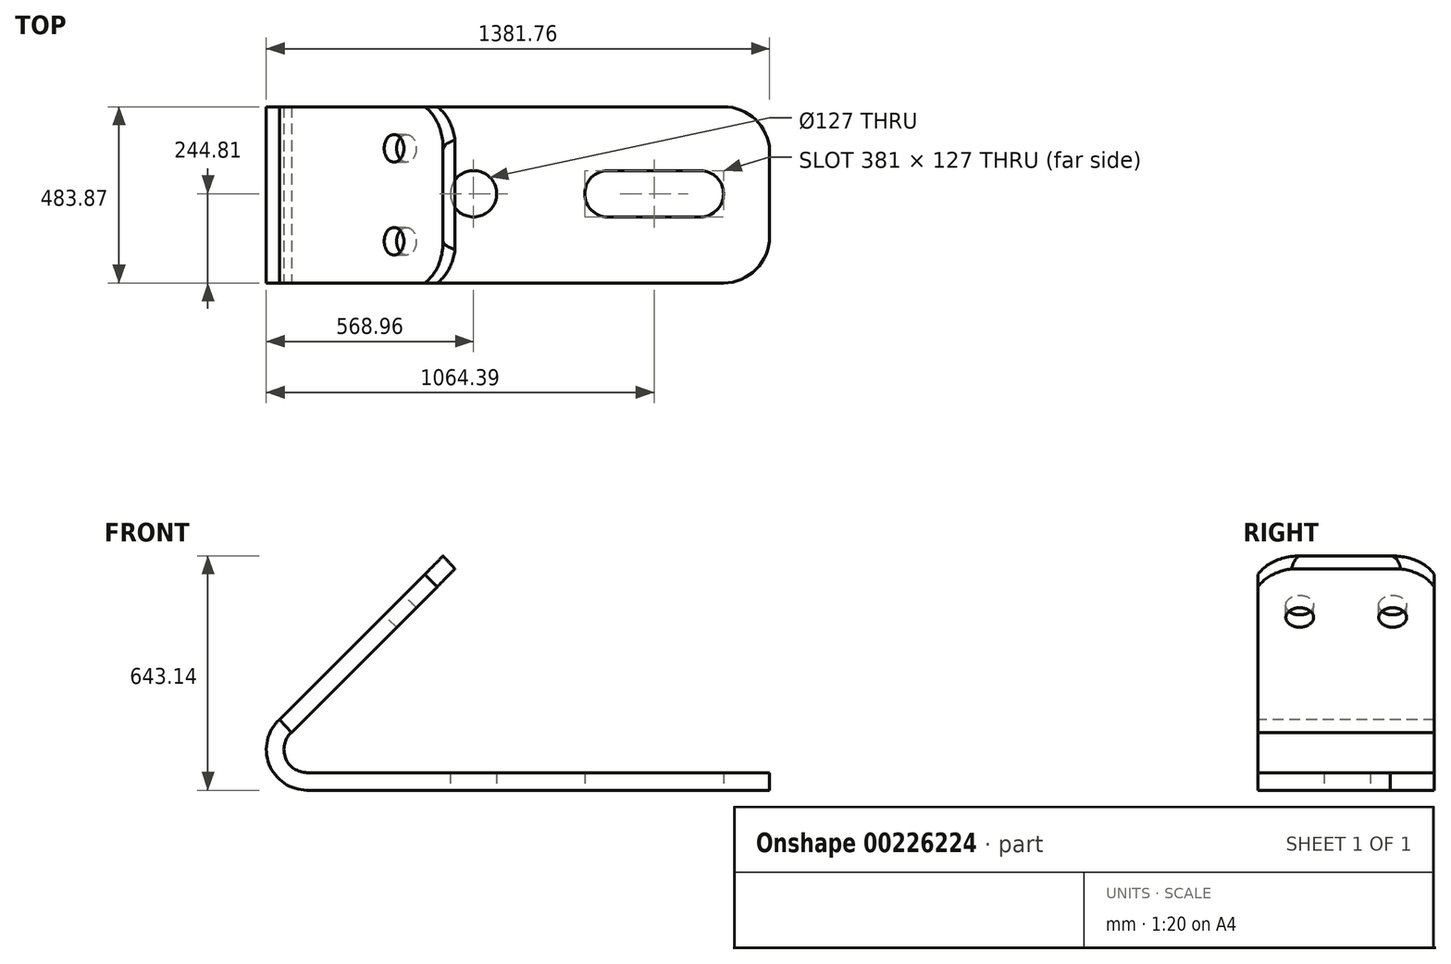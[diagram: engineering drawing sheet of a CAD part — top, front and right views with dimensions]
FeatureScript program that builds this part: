
annotation { "Feature Type Name" : "Feature", "Feature Type Description" : "" }
export const myFeature = defineFeature(function(context is Context, id is Id, definition is map)
    precondition{}
    {
        {
            var Q0;
            Q0=qCreatedBy(makeId("Top.planeOp"),FACE);
            var sketch = newSketch(context, id + "F0", { "sketchPlane" : qUnion([Q0])});
            skLineSegment(sketch, "E0", {"start": v(-457.2, 239.06) * mm, "end": v(-457.2, -244.8) * mm});
            skLineSegment(sketch, "E1", {"start": v(-457.2, -244.8) * mm, "end": v(685.93, -244.8) * mm});
            skLineSegment(sketch, "E2", {"start": v(-457.2, 239.06) * mm, "end": v(685.93, 239.06) * mm});
            skLineSegment(sketch, "E3", {"start": v(812.8, 117.8) * mm, "end": v(812.8, -117.8) * mm});
            skArc(sketch, "E4", {"start": v(812.8, 117.8) * mm, "mid": v(773.68, 203.87) * mm, "end": v(685.93, 239.06) * mm});
            skArc(sketch, "E5", {"start": v(685.93, -244.8) * mm, "mid": v(775.65, -207.56) * mm, "end": v(812.8, -117.8) * mm});
            skCircle(sketch, "E6", {"center": v(0, 0) * mm, "radius": 63.5 * mm});
            skLineSegment(sketch, "E7", {"start": v(0, 0) * mm, "end": v(908.2, 0) * mm, "construction": true});
            skLineSegment(sketch, "E8.bottom", {"start": v(368.43, 63.5) * mm, "end": v(622.43, 63.5) * mm});
            skLineSegment(sketch, "E8.top", {"start": v(368.43, -63.5) * mm, "end": v(622.43, -63.5) * mm});
            skPoint(sketch, "E8.middle", {"position": v(495.43, 0) * mm});
            skArc(sketch, "E9", {"start": v(368.43, 63.5) * mm, "mid": v(304.93, 0) * mm, "end": v(368.43, -63.5) * mm});
            skArc(sketch, "E10", {"start": v(622.43, -63.5) * mm, "mid": v(685.93, 0) * mm, "end": v(622.43, 63.5) * mm});
            skSolve(sketch);
        }
        {
            var Q0;
            Q0=makeQuery(id+"F0.imprint","IMPRINT",FACE,{"disambiguationData":[TD([[makeQuery(id+"F0.imprint","IMPRINT",EDGE,{"derivedFrom":sQuery(id+"F0.wireOp",EDGE,"E0")}),1.0]])]});
            extrude(context, id + "F1", {"entities" : qUnion([Q0]), "depth" : 48.26 * mm});
        }
        {
            var Q0;
            Q0=makeQuery(id+"F1.opExtrude","SWEPT_FACE",FACE,{"disambiguationData":[OSD([sQuery(id+"F0.wireOp",EDGE,"E1")])]});
            var sketch = newSketch(context, id + "F2", { "sketchPlane" : qUnion([Q0])});
            skArc(sketch, "E11", {"start": v(-532.74, 194.13) * mm, "mid": v(-561.35, 71.23) * mm, "end": v(-457.2, 0) * mm});
            skArc(sketch, "E12", {"start": v(-500.12, 158.56) * mm, "mid": v(-516.38, 88.73) * mm, "end": v(-457.2, 48.26) * mm});
            skLineSegment(sketch, "E13", {"start": v(-532.74, 194.13) * mm, "end": v(-500.12, 158.56) * mm});
            skSolve(sketch);
        }
        {
            var Q0;
            Q0 = qSketchRegion(id + "F2", true);
            var Q1;
            Q1=makeQuery(id+"F2.imprint","IMPRINT",FACE,{"disambiguationData":[TD([[makeQuery(id+"F2.imprint","IMPRINT",EDGE,{"derivedFrom":sQuery(id+"F2.wireOp",EDGE,"E11")}),1.0]])]});
            extrude(context, id + "F3", {"entities" : qUnion([Q0, Q1]), "oppositeDirection" : true, "depth" : 483.87 * mm});
        }
        {
            var Q0;
            Q0 = qSketchRegion(id + "F2", true);
            var Q1;
            Q1=makeQuery(id+"F3.opExtrude","CAP_FACE",FACE,{"disambiguationData":[OSD([sQuery(id+"F0.wireOp",EDGE,"E0"),sQuery(id+"F0.wireOp",EDGE,"E1"),sQuery(id+"F2.wireOp",EDGE,"E11"),sQuery(id+"F2.wireOp",EDGE,"E12"),sQuery(id+"F2.wireOp",EDGE,"E13")])],"isStart":true});
            extrude(context, id + "F4", {"entities" : qUnion([Q0, Q1]), "operationType" : NewBodyOperationType.ADD, "oppositeDirection" : true, "depth" : 483.87 * mm});
        }
        {
            var Q0;
            Q0=makeQuery(id+"F3.opExtrude","CAP_FACE",FACE,{"disambiguationData":[OSD([sQuery(id+"F0.wireOp",EDGE,"E0"),sQuery(id+"F0.wireOp",EDGE,"E1"),sQuery(id+"F2.wireOp",EDGE,"E11"),sQuery(id+"F2.wireOp",EDGE,"E12"),sQuery(id+"F2.wireOp",EDGE,"E13")])],"isStart":true});
            var sketch = newSketch(context, id + "F5", { "sketchPlane" : qUnion([Q0])});
            skLineSegment(sketch, "E14", {"start": v(-532.74, 194.13) * mm, "end": v(-500.12, 158.56) * mm});
            skLineSegment(sketch, "E15", {"start": v(-500.12, 158.56) * mm, "end": v(-532.74, 194.13) * mm});
            skLineSegment(sketch, "E16", {"start": v(-532.74, 194.13) * mm, "end": v(-83.73, 643.14) * mm});
            skPoint(sketch, "E17.end.orphan", {"position": v(0, 658.68) * mm});
            skLineSegment(sketch, "E18", {"start": v(-500.12, 158.56) * mm, "end": v(-51.1, 607.57) * mm});
            skLineSegment(sketch, "E19", {"start": v(-83.73, 643.14) * mm, "end": v(-51.1, 607.57) * mm});
            skSolve(sketch);
        }
        {
            var Q0;
            Q0 = qSketchRegion(id + "F5", true);
            extrude(context, id + "F6", {"entities" : qUnion([Q0]), "oppositeDirection" : true, "depth" : 483.87 * mm});
        }
        {
            var Q0;
            Q0=makeQuery(id+"F6.opExtrude","SWEPT_FACE",FACE,{"disambiguationData":[OSD([sQuery(id+"F5.wireOp",EDGE,"E16")])]});
            var sketch = newSketch(context, id + "F7", { "sketchPlane" : qUnion([Q0])});
            skLineSegment(sketch, "E20", {"start": v(2.87, 395.56) * mm, "end": v(130.5, 395.56) * mm});
            skLineSegment(sketch, "E21", {"start": v(2.87, 395.56) * mm, "end": v(-124.76, 395.56) * mm});
            skArc(sketch, "E22", {"start": v(-124.76, 395.56) * mm, "mid": v(-129.42, 395.48) * mm, "end": v(-134.07, 395.22) * mm});
            skArc(sketch, "E23", {"start": v(244.8, 323.92) * mm, "mid": v(197.96, 376.17) * mm, "end": v(130.5, 395.56) * mm});
            skCircle(sketch, "E24", {"center": v(-124.76, 205.06) * mm, "radius": 38.1 * mm});
            skCircle(sketch, "E25", {"center": v(130.5, 205.06) * mm, "radius": 38.1 * mm});
            skLineSegment(sketch, "E26", {"start": v(-239.06, 323.92) * mm, "end": v(-239.06, 395.56) * mm});
            skLineSegment(sketch, "E27", {"start": v(-134.07, 395.22) * mm, "end": v(-124.76, 395.56) * mm});
            skLineSegment(sketch, "E28", {"start": v(130.5, 395.56) * mm, "end": v(244.8, 395.56) * mm});
            skLineSegment(sketch, "E29", {"start": v(244.8, 395.56) * mm, "end": v(244.8, 323.92) * mm});
            skLineSegment(sketch, "E30", {"start": v(-239.06, 395.56) * mm, "end": v(-124.76, 395.56) * mm});
            skArc(sketch, "E31", {"start": v(-124.76, 395.56) * mm, "mid": v(-192.21, 376.17) * mm, "end": v(-239.06, 323.92) * mm});
            skSolve(sketch);
        }
        {
            var Q0;
            Q0=makeQuery(id+"F7.imprint","IMPRINT",FACE,{"disambiguationData":[TD([[makeQuery(id+"F7.imprint","IMPRINT",EDGE,{"derivedFrom":sQuery(id+"F7.wireOp",EDGE,"E23")}),-1.0]])]});
            var Q1;
            Q1=makeQuery(id+"F7.imprint","IMPRINT",FACE,{"disambiguationData":[TD([[makeQuery(id+"F7.imprint","IMPRINT",EDGE,{"derivedFrom":sQuery(id+"F7.wireOp",EDGE,"E24")}),1.0]])]});
            var Q2;
            Q2=makeQuery(id+"F7.imprint","IMPRINT",FACE,{"disambiguationData":[TD([[makeQuery(id+"F7.imprint","IMPRINT",EDGE,{"derivedFrom":sQuery(id+"F7.wireOp",EDGE,"E25")}),1.0]])]});
            var Q3;
            {var subQ0=sQuery(id+"F7.wireOp",EDGE,"E27");Q3=makeQuery(id+"F7.imprint","IMPRINT",FACE,{"disambiguationData":[TD([[makeQuery(id+"F7.imprint","IMPRINT",EDGE,{"derivedFrom":subQ0}),1.0]])]});}
            var Q4;
            {var subQ0=sQuery(id+"F7.wireOp",EDGE,"E26");Q4=makeQuery(id+"F7.imprint","IMPRINT",FACE,{"disambiguationData":[TD([[makeQuery(id+"F7.imprint","IMPRINT",EDGE,{"derivedFrom":subQ0}),-1.0]])]});}
            extrude(context, id + "F8", {"entities" : qUnion([Q0, Q1, Q2, Q3, Q4]), "operationType" : NewBodyOperationType.REMOVE, "oppositeDirection" : true, "depth" : 48.26 * mm});
        }
    });
